# Revit family: Casement_41_B_Side_Hung_SD_Standard
name_source: partatom
category: Windows
revit_build: Autodesk Revit 2014 (Build: 20130308_1515(x64)
units: mm (PartAtom-declared; Revit-internal decimal feet)

## types (18) — shared parameters
Corrected Mullion Configuration = 2 mm  [stored 0.00656168 ft]
Custom Sash Width = 502 mm
Description = Window 41mm, Type B, Side hung, Standard sash
Frame Profile Thickness = 41 mm  [stored 0.134514 ft]
Heavy Duty Sash = No
Limit Fixed Pane Height Max = 3000 mm  [stored 9.84252 ft]
Limit Fixed Pane Height Min = 200 mm  [stored 0.656168 ft]
Limit Fixed Pane Width Max = 3000 mm  [stored 9.84252 ft]
Limit Fixed Pane Width Min = 200 mm  [stored 0.656168 ft]
Limit Sash Height Max = 1500 mm  [stored 4.92126 ft]
Limit Sash Height Min = 300 mm  [stored 0.984252 ft]
Limit Sash Width Max = 700 mm  [stored 2.29659 ft]
Limit Sash Width Min = 300 mm  [stored 0.984252 ft]
Limit Window Height Max = 1588 mm
Limit Window Height Min = 388 mm
Manufacturer = Crealco
Max System DG Unit Thickness = 25 mm  [stored 0.082021 ft]
Model = Casement 41
Rough Width = 3 mm  [stored 0.00984252 ft]
Sash Side Gap = 44 mm
Standard Mullion Different = No
Standard Sash = Yes
URL = http://www.crealco.co.za
Wall Closure = By host
zero-valued in all types: Custom Frame Offset From Exterior

## per-type parameters (varying)
| type | Clearvue Insulated LowE SHGC Value | Clearvue Insulated LowE U Value | Clearvue Insulated SHGC Value | Clearvue Insulated U Value | Clearvue SHGC Value | Clearvue U Value | Custom Windload | Custom Window Height | Custom Window Width | Energy Advantage SHGC Value | Energy Advantage U Value | Intruderprufe Insulated LowE SHGC Value | Intruderprufe Insulated LowE U Value | Intruderprufe Insulated SHGC Value | Intruderprufe Insulated U Value | Intruderprufe LowE SHGC Value | Intruderprufe LowE U Value | Intruderprufe SHGC Value | Intruderprufe U Value | Toughened Safety SHGC Value | Toughened Safety U Value |
| 41-0909S-SD-1000Pa | 0.736 | 4.1 | 0.736 | 4.18 | 0.497 | 6.07 | 1000 mm  [stored 3.28084 ft] | 890 mm  [stored 2.91995 ft] | 890 mm  [stored 2.91995 ft] | 0.448 | 5.06 | 0.611 | 2.98 | 0.611 | 3.04 | 0.417 | 4.9 | 0.469 | 5.92 | 0.479 | 6.07 |
| 41-0909S-SD-1500Pa | 0.736 | 4.1 | 0.736 | 4.18 | 0.497 | 6.07 | 1500 mm  [stored 4.92126 ft] | 890 mm  [stored 2.91995 ft] | 890 mm  [stored 2.91995 ft] | 0.448 | 5.06 | 0.611 | 2.98 | 0.611 | 3.04 | 0.417 | 4.9 | 0.469 | 5.92 | 0.479 | 6.07 |
| 41-0909S-SD-2000Pa | 0.736 | 4.1 | 0.736 | 4.18 | 0.497 | 6.07 | 2000 mm  [stored 6.56168 ft] | 890 mm  [stored 2.91995 ft] | 890 mm  [stored 2.91995 ft] | 0.448 | 5.06 | 0.611 | 2.98 | 0.611 | 3.04 | 0.417 | 4.9 | 0.469 | 5.92 | 0.479 | 6.07 |
| 41-1209S-SD-1000Pa | 0.765 | 4.33 | 0.765 | 4.4 | 0.56 | 6.05 | 1000 mm  [stored 3.28084 ft] | 890 mm  [stored 2.91995 ft] | 1190 mm  [stored 3.9042 ft] | 0.503 | 4.83 | 0.635 | 3.01 | 0.635 | 3.06 | 0.468 | 4.67 | 0.527 | 5.87 | 0.56 | 6.05 |
| 41-1209S-SD-1500Pa | 0.765 | 4.33 | 0.765 | 4.4 | 0.56 | 6.05 | 1500 mm  [stored 4.92126 ft] | 890 mm  [stored 2.91995 ft] | 1190 mm  [stored 3.9042 ft] | 0.503 | 4.83 | 0.635 | 3.01 | 0.635 | 3.06 | 0.468 | 4.67 | 0.527 | 5.87 | 0.56 | 6.05 |
| 41-1209S-SD-2000Pa | 0.765 | 4.33 | 0.765 | 4.4 | 0.56 | 6.05 | 2000 mm  [stored 6.56168 ft] | 890 mm  [stored 2.91995 ft] | 1190 mm  [stored 3.9042 ft] | 0.503 | 4.83 | 0.635 | 3.01 | 0.635 | 3.06 | 0.468 | 4.67 | 0.527 | 5.87 | 0.56 | 6.05 |
| 41-1509S-SD-1000Pa | 0.782 | 4.48 | 0.782 | 4.53 | 0.597 | 6.03 | 1000 mm  [stored 3.28084 ft] | 890 mm  [stored 2.91995 ft] | 1490 mm  [stored 4.88845 ft] | 0.536 | 4.69 | 0.649 | 3.03 | 0.649 | 3.07 | 0.498 | 4.53 | 0.562 | 5.85 | 0.597 | 6.03 |
| 41-1509S-SD-1500Pa | 0.782 | 4.48 | 0.782 | 4.53 | 0.597 | 6.03 | 1500 mm  [stored 4.92126 ft] | 890 mm  [stored 2.91995 ft] | 1490 mm  [stored 4.88845 ft] | 0.536 | 4.69 | 0.649 | 3.03 | 0.649 | 3.07 | 0.498 | 4.53 | 0.562 | 5.85 | 0.597 | 6.03 |
| 41-1509S-SD-2000Pa | 0.782 | 4.48 | 0.782 | 4.53 | 0.597 | 6.03 | 2000 mm  [stored 6.56168 ft] | 890 mm  [stored 2.91995 ft] | 1490 mm  [stored 4.88845 ft] | 0.536 | 4.69 | 0.649 | 3.03 | 0.649 | 3.07 | 0.498 | 4.53 | 0.562 | 5.85 | 0.597 | 6.03 |
| 41-0912S-SD-1000Pa | 0.736 | 4.24 | 0.736 | 4.33 | 0.523 | 6.05 | 1000 mm  [stored 3.28084 ft] | 1190 mm  [stored 3.9042 ft] | 890 mm  [stored 2.91995 ft] | 0.471 | 4.95 | 0.612 | 3.08 | 0.612 | 3.14 | 0.438 | 4.81 | 0.493 | 5.9 | 0.523 | 6.05 |
| 41-0912S-SD-1500Pa | 0.736 | 4.24 | 0.736 | 4.33 | 0.523 | 6.05 | 1500 mm  [stored 4.92126 ft] | 1190 mm  [stored 3.9042 ft] | 890 mm  [stored 2.91995 ft] | 0.471 | 4.95 | 0.612 | 3.08 | 0.612 | 3.14 | 0.438 | 4.81 | 0.493 | 5.9 | 0.523 | 6.05 |
| 41-0912S-SD-2000Pa | 0.736 | 4.24 | 0.736 | 4.33 | 0.523 | 6.05 | 2000 mm  [stored 6.56168 ft] | 1190 mm  [stored 3.9042 ft] | 890 mm  [stored 2.91995 ft] | 0.471 | 4.95 | 0.612 | 3.08 | 0.612 | 3.14 | 0.438 | 4.81 | 0.493 | 5.9 | 0.523 | 6.05 |
| 41-1212S-SD-1000Pa | 0.765 | 4.5 | 0.765 | 4.56 | 0.585 | 6.03 | 1000 mm  [stored 3.28084 ft] | 1190 mm  [stored 3.9042 ft] | 1190 mm  [stored 3.9042 ft] | 0.526 | 4.72 | 0.635 | 3.12 | 0.635 | 3.16 | 0.489 | 4.58 | 0.551 | 5.86 | 0.585 | 6.03 |
| 41-1212S-SD-1500Pa | 0.765 | 4.5 | 0.765 | 4.56 | 0.585 | 6.03 | 1500 mm  [stored 4.92126 ft] | 1190 mm  [stored 3.9042 ft] | 1190 mm  [stored 3.9042 ft] | 0.526 | 4.72 | 0.635 | 3.12 | 0.635 | 3.16 | 0.489 | 4.58 | 0.551 | 5.86 | 0.585 | 6.03 |
| 41-1212S-SD-2000Pa | 0.765 | 4.5 | 0.765 | 4.56 | 0.585 | 6.03 | 2000 mm  [stored 6.56168 ft] | 1190 mm  [stored 3.9042 ft] | 1190 mm  [stored 3.9042 ft] | 0.526 | 4.72 | 0.635 | 3.12 | 0.635 | 3.16 | 0.489 | 4.58 | 0.551 | 5.86 | 0.585 | 6.03 |
| 41-1512S-SD-1000Pa | 0.782 | 4.65 | 0.782 | 4.7 | 0.623 | 6.01 | 1000 mm  [stored 3.28084 ft] | 1190 mm  [stored 3.9042 ft] | 1490 mm  [stored 4.88845 ft] | 0.559 | 4.58 | 0.649 | 3.15 | 0.649 | 3.18 | 0.519 | 4.44 | 0.586 | 5.84 | 0.623 | 6.01 |
| 41-1512S-SD-1500Pa | 0.782 | 4.65 | 0.782 | 4.7 | 0.623 | 6.01 | 1500 mm  [stored 4.92126 ft] | 1190 mm  [stored 3.9042 ft] | 1490 mm  [stored 4.88845 ft] | 0.559 | 4.58 | 0.649 | 3.15 | 0.649 | 3.18 | 0.519 | 4.44 | 0.586 | 5.84 | 0.623 | 6.01 |
| 41-1512S-SD-2000Pa | 0.782 | 4.65 | 0.782 | 4.7 | 0.623 | 6.01 | 2000 mm  [stored 6.56168 ft] | 1190 mm  [stored 3.9042 ft] | 1490 mm  [stored 4.88845 ft] | 0.559 | 4.58 | 0.649 | 3.15 | 0.649 | 3.18 | 0.519 | 4.44 | 0.586 | 5.84 | 0.623 | 6.01 |

note: [stored X ft] marks values corroborated as IEEE doubles in the binary element streams (Revit-internal decimal feet)

## geometry (parser evidence)
native form markers: Sweep x22
no freeform markers — native parametric forms only
